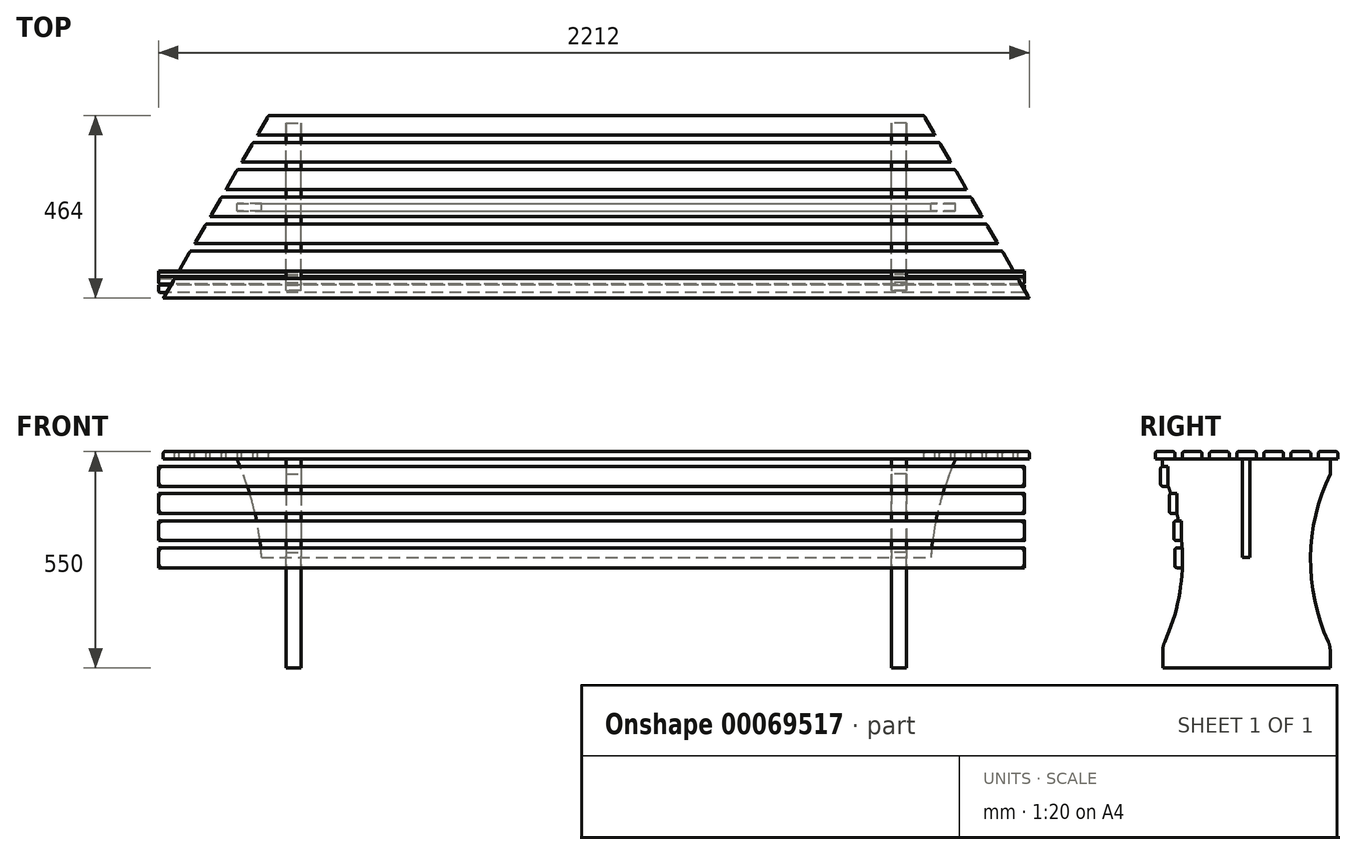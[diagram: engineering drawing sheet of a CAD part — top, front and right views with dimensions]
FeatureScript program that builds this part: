
annotation { "Feature Type Name" : "Feature", "Feature Type Description" : "" }
export const myFeature = defineFeature(function(context is Context, id is Id, definition is map)
    precondition{}
    {
        {
            var Q0;
            Q0=qCreatedBy(makeId("Top.planeOp"),FACE);
            var sketch = newSketch(context, id + "F0", { "sketchPlane" : qUnion([Q0])});
            skLineSegment(sketch, "E0.bottom", {"start": v(-1100, 50) * mm, "end": v(1100, 50) * mm});
            skLineSegment(sketch, "E0.top", {"start": v(-1100, 0) * mm, "end": v(1100, 0) * mm});
            skLineSegment(sketch, "E0.left", {"start": v(-1100, 50) * mm, "end": v(-1100, 0) * mm});
            skLineSegment(sketch, "E0.right", {"start": v(1100, 50) * mm, "end": v(1100, 0) * mm});
            skLineSegment(sketch, "E1.bottom", {"start": v(-1100, 119) * mm, "end": v(1100, 119) * mm});
            skLineSegment(sketch, "E1.top", {"start": v(-1100, 69) * mm, "end": v(1100, 69) * mm});
            skLineSegment(sketch, "E1.left", {"start": v(-1100, 119) * mm, "end": v(-1100, 69) * mm});
            skLineSegment(sketch, "E1.right", {"start": v(1100, 119) * mm, "end": v(1100, 69) * mm});
            skLineSegment(sketch, "E2.bottom", {"start": v(-1100, 188) * mm, "end": v(1100, 188) * mm});
            skLineSegment(sketch, "E2.top", {"start": v(-1100, 138) * mm, "end": v(1100, 138) * mm});
            skLineSegment(sketch, "E2.left", {"start": v(-1100, 188) * mm, "end": v(-1100, 138) * mm});
            skLineSegment(sketch, "E2.right", {"start": v(1100, 188) * mm, "end": v(1100, 138) * mm});
            skLineSegment(sketch, "E3.bottom", {"start": v(-1100, 257) * mm, "end": v(1100, 257) * mm});
            skLineSegment(sketch, "E3.top", {"start": v(-1100, 207) * mm, "end": v(1100, 207) * mm});
            skLineSegment(sketch, "E3.left", {"start": v(-1100, 257) * mm, "end": v(-1100, 207) * mm});
            skLineSegment(sketch, "E3.right", {"start": v(1100, 257) * mm, "end": v(1100, 207) * mm});
            skLineSegment(sketch, "E4.bottom", {"start": v(-1100, 326) * mm, "end": v(1100, 326) * mm});
            skLineSegment(sketch, "E4.top", {"start": v(-1100, 276) * mm, "end": v(1100, 276) * mm});
            skLineSegment(sketch, "E4.left", {"start": v(-1100, 326) * mm, "end": v(-1100, 276) * mm});
            skLineSegment(sketch, "E4.right", {"start": v(1100, 326) * mm, "end": v(1100, 276) * mm});
            skLineSegment(sketch, "E5.bottom", {"start": v(-1100, 395) * mm, "end": v(1100, 395) * mm});
            skLineSegment(sketch, "E5.top", {"start": v(-1100, 345) * mm, "end": v(1100, 345) * mm});
            skLineSegment(sketch, "E5.left", {"start": v(-1100, 395) * mm, "end": v(-1100, 345) * mm});
            skLineSegment(sketch, "E5.right", {"start": v(1100, 395) * mm, "end": v(1100, 345) * mm});
            skLineSegment(sketch, "E6.bottom", {"start": v(-1100, 464) * mm, "end": v(1100, 464) * mm});
            skLineSegment(sketch, "E6.top", {"start": v(-1100, 414) * mm, "end": v(1100, 414) * mm});
            skLineSegment(sketch, "E6.left", {"start": v(-1100, 464) * mm, "end": v(-1100, 414) * mm});
            skLineSegment(sketch, "E6.right", {"start": v(1100, 464) * mm, "end": v(1100, 414) * mm});
            skSolve(sketch);
        }
        {
            var Q0;
            Q0=makeQuery(id+"F0.imprint","IMPRINT",FACE,{"disambiguationData":[TD([[makeQuery(id+"F0.imprint","IMPRINT",EDGE,{"derivedFrom":sQuery(id+"F0.wireOp",EDGE,"E0.bottom")}),-1.0]])]});
            var Q1;
            Q1=makeQuery(id+"F0.imprint","IMPRINT",FACE,{"disambiguationData":[TD([[makeQuery(id+"F0.imprint","IMPRINT",EDGE,{"derivedFrom":sQuery(id+"F0.wireOp",EDGE,"E1.bottom")}),-1.0]])]});
            var Q2;
            Q2=makeQuery(id+"F0.imprint","IMPRINT",FACE,{"disambiguationData":[TD([[makeQuery(id+"F0.imprint","IMPRINT",EDGE,{"derivedFrom":sQuery(id+"F0.wireOp",EDGE,"E2.bottom")}),-1.0]])]});
            var Q3;
            Q3=makeQuery(id+"F0.imprint","IMPRINT",FACE,{"disambiguationData":[TD([[makeQuery(id+"F0.imprint","IMPRINT",EDGE,{"derivedFrom":sQuery(id+"F0.wireOp",EDGE,"E3.bottom")}),-1.0]])]});
            var Q4;
            Q4=makeQuery(id+"F0.imprint","IMPRINT",FACE,{"disambiguationData":[TD([[makeQuery(id+"F0.imprint","IMPRINT",EDGE,{"derivedFrom":sQuery(id+"F0.wireOp",EDGE,"E4.bottom")}),-1.0]])]});
            var Q5;
            Q5=makeQuery(id+"F0.imprint","IMPRINT",FACE,{"disambiguationData":[TD([[makeQuery(id+"F0.imprint","IMPRINT",EDGE,{"derivedFrom":sQuery(id+"F0.wireOp",EDGE,"E5.bottom")}),-1.0]])]});
            var Q6;
            Q6=makeQuery(id+"F0.imprint","IMPRINT",FACE,{"disambiguationData":[TD([[makeQuery(id+"F0.imprint","IMPRINT",EDGE,{"derivedFrom":sQuery(id+"F0.wireOp",EDGE,"E6.bottom")}),-1.0]])]});
            extrude(context, id + "F1", {"entities" : qUnion([Q0, Q1, Q2, Q3, Q4, Q5, Q6]), "depth" : 19 * mm});
        }
        {
            var Q0;
            Q0=qCreatedBy(makeId("Right.planeOp"),FACE);
            cPlane(context, id + "F2", {"entities" : qUnion([Q0]), "cplaneType" : CPlaneType.OFFSET, "offset" : 750 * mm, "width" : 150 * mm, "height" : 150 * mm});
        }
        {
            var Q0;
            Q0=qCreatedBy(id+"F2.planeOp",FACE);
            var sketch = newSketch(context, id + "F3", { "sketchPlane" : qUnion([Q0])});
            skLineSegment(sketch, "E7", {"start": v(19, 0) * mm, "end": v(445, 0) * mm});
            skLineSegment(sketch, "E8", {"start": v(445, 0) * mm, "end": v(445, -38) * mm});
            skLineSegment(sketch, "E9", {"start": v(19, 0) * mm, "end": v(19, -38) * mm});
            skArc(sketch, "E10", {"start": v(19.5, -474) * mm, "mid": v(69.28, -255.94) * mm, "end": v(19, -38) * mm});
            skArc(sketch, "E11", {"start": v(445, -38) * mm, "mid": v(394.72, -255.94) * mm, "end": v(444.5, -474) * mm});
            skLineSegment(sketch, "E12", {"start": v(19.5, -474) * mm, "end": v(19.5, -531) * mm});
            skLineSegment(sketch, "E13", {"start": v(19.5, -531) * mm, "end": v(444.5, -531) * mm});
            skLineSegment(sketch, "E14", {"start": v(444.5, -531) * mm, "end": v(444.5, -474) * mm});
            skSolve(sketch);
        }
        {
            var Q0;
            Q0=makeQuery(id+"F3.imprint","IMPRINT",FACE,{"disambiguationData":[TD([[makeQuery(id+"F3.imprint","IMPRINT",EDGE,{"derivedFrom":sQuery(id+"F3.wireOp",EDGE,"E7")}),-1.0]])]});
            extrude(context, id + "F4", {"entities" : qUnion([Q0]), "depth" : 38 * mm});
        }
        {
            var Q0;
            Q0=makeQuery(id+"F4.opExtrude","SWEPT_BODY",BODY,{"disambiguationData":[OSD([sQuery(id+"F3.wireOp",EDGE,"E7"),sQuery(id+"F3.wireOp",EDGE,"E8"),sQuery(id+"F3.wireOp",EDGE,"E9"),sQuery(id+"F3.wireOp",EDGE,"E10"),sQuery(id+"F3.wireOp",EDGE,"E11"),sQuery(id+"F3.wireOp",EDGE,"E12"),sQuery(id+"F3.wireOp",EDGE,"E13"),sQuery(id+"F3.wireOp",EDGE,"E14")])]});
            var Q1;
            Q1=qCreatedBy(makeId("Right.planeOp"),FACE);
            mirror(context, id + "F5", {"entities" : qUnion([Q0]), "mirrorPlane" : qUnion([Q1])});
        }
        {
            var Q0;
            Q0=qCreatedBy(makeId("Front.planeOp"),FACE);
            cPlane(context, id + "F6", {"entities" : qUnion([Q0]), "cplaneType" : CPlaneType.OFFSET, "offset" : 240 * mm, "oppositeDirection" : true, "width" : 150 * mm, "height" : 150 * mm});
        }
        {
            var Q0;
            Q0=qCreatedBy(id+"F6.planeOp",FACE);
            var sketch = newSketch(context, id + "F7", { "sketchPlane" : qUnion([Q0])});
            skLineSegment(sketch, "E15", {"start": v(-913, 0) * mm, "end": v(913, 0) * mm});
            skArc(sketch, "E16", {"start": v(-850, -250) * mm, "mid": v(-870.68, -122.27) * mm, "end": v(-913, 0) * mm});
            skArc(sketch, "E17", {"start": v(913, 0) * mm, "mid": v(870.68, -122.27) * mm, "end": v(850, -250) * mm});
            skLineSegment(sketch, "E18", {"start": v(-850, -250) * mm, "end": v(850, -250) * mm});
            skSolve(sketch);
        }
        {
            var Q0;
            Q0=makeQuery(id+"F7.imprint","IMPRINT",FACE,{"disambiguationData":[TD([[makeQuery(id+"F7.imprint","IMPRINT",EDGE,{"derivedFrom":sQuery(id+"F7.wireOp",EDGE,"E15")}),-1.0]])]});
            extrude(context, id + "F8", {"entities" : qUnion([Q0]), "depth" : 19 * mm});
        }
        {
            var Q0;
            Q0=makeQuery(id+"F1.opExtrude","CAP_FACE",FACE,{"disambiguationData":[OSD([sQuery(id+"F0.wireOp",EDGE,"E6.bottom"),sQuery(id+"F0.wireOp",EDGE,"E6.top"),sQuery(id+"F0.wireOp",EDGE,"E6.left"),sQuery(id+"F0.wireOp",EDGE,"E6.right")])],"isStart":false});
            var sketch = newSketch(context, id + "F9", { "sketchPlane" : qUnion([Q0])});
            skLineSegment(sketch, "E19", {"start": v(-1100, 0) * mm, "end": v(-1100, 464) * mm});
            skLineSegment(sketch, "E20", {"start": v(-1100, 464) * mm, "end": v(-832.1, 464) * mm});
            skLineSegment(sketch, "E21", {"start": v(-832.1, 464) * mm, "end": v(-1100, 0) * mm});
            skLineSegment(sketch, "E22", {"start": v(1100, 0) * mm, "end": v(1100, 464) * mm});
            skLineSegment(sketch, "E23", {"start": v(1100, 464) * mm, "end": v(832.1, 464) * mm});
            skLineSegment(sketch, "E24", {"start": v(832.1, 464) * mm, "end": v(1100, 0) * mm});
            skSolve(sketch);
        }
        {
            var Q0;
            Q0 = qSketchRegion(id + "F9", true);
            extrude(context, id + "F10", {"entities" : qUnion([Q0]), "operationType" : NewBodyOperationType.REMOVE, "endBound" : BoundingType.THROUGH_ALL, "oppositeDirection" : true, "depth" : 25 * mm});
        }
        {
            var Q0;
            Q0=makeQuery(id+"F1.opExtrude","CAP_EDGE",EDGE,{"disambiguationData":[OSD([sQuery(id+"F0.wireOp",EDGE,"E0.top")])],"isStart":false});
            var Q1;
            Q1=makeQuery(id+"F10.boolean.opBoolean","COPY",EDGE,{"disambiguationData":[OD(0.0)],"derivedFrom":makeQuery(id+"F10.opExtrude","CAP_EDGE",EDGE,{"disambiguationData":[OSD([sQuery(id+"F9.wireOp",EDGE,"E24")])],"isStart":true})});
            var Q2;
            Q2=makeQuery(id+"F1.opExtrude","CAP_EDGE",EDGE,{"disambiguationData":[OSD([sQuery(id+"F0.wireOp",EDGE,"E0.bottom")])],"isStart":false});
            var Q3;
            Q3=makeQuery(id+"F1.opExtrude","CAP_EDGE",EDGE,{"disambiguationData":[OSD([sQuery(id+"F0.wireOp",EDGE,"E1.top")])],"isStart":false});
            var Q4;
            Q4=makeQuery(id+"F10.boolean.opBoolean","COPY",EDGE,{"disambiguationData":[OD(2.0)],"derivedFrom":makeQuery(id+"F10.opExtrude","CAP_EDGE",EDGE,{"disambiguationData":[OSD([sQuery(id+"F9.wireOp",EDGE,"E24")])],"isStart":true})});
            var Q5;
            Q5=makeQuery(id+"F1.opExtrude","CAP_EDGE",EDGE,{"disambiguationData":[OSD([sQuery(id+"F0.wireOp",EDGE,"E1.bottom")])],"isStart":false});
            var Q6;
            Q6=makeQuery(id+"F1.opExtrude","CAP_EDGE",EDGE,{"disambiguationData":[OSD([sQuery(id+"F0.wireOp",EDGE,"E2.top")])],"isStart":false});
            var Q7;
            Q7=makeQuery(id+"F10.boolean.opBoolean","COPY",EDGE,{"disambiguationData":[OD(3.0)],"derivedFrom":makeQuery(id+"F10.opExtrude","CAP_EDGE",EDGE,{"disambiguationData":[OSD([sQuery(id+"F9.wireOp",EDGE,"E24")])],"isStart":true})});
            var Q8;
            Q8=makeQuery(id+"F1.opExtrude","CAP_EDGE",EDGE,{"disambiguationData":[OSD([sQuery(id+"F0.wireOp",EDGE,"E2.bottom")])],"isStart":false});
            var Q9;
            Q9=makeQuery(id+"F1.opExtrude","CAP_EDGE",EDGE,{"disambiguationData":[OSD([sQuery(id+"F0.wireOp",EDGE,"E3.top")])],"isStart":false});
            var Q10;
            Q10=makeQuery(id+"F1.opExtrude","CAP_EDGE",EDGE,{"disambiguationData":[OSD([sQuery(id+"F0.wireOp",EDGE,"E3.bottom")])],"isStart":false});
            var Q11;
            Q11=makeQuery(id+"F10.boolean.opBoolean","COPY",EDGE,{"disambiguationData":[OD(4.0)],"derivedFrom":makeQuery(id+"F10.opExtrude","CAP_EDGE",EDGE,{"disambiguationData":[OSD([sQuery(id+"F9.wireOp",EDGE,"E24")])],"isStart":true})});
            var Q12;
            Q12=makeQuery(id+"F1.opExtrude","CAP_EDGE",EDGE,{"disambiguationData":[OSD([sQuery(id+"F0.wireOp",EDGE,"E4.top")])],"isStart":false});
            var Q13;
            Q13=makeQuery(id+"F1.opExtrude","CAP_EDGE",EDGE,{"disambiguationData":[OSD([sQuery(id+"F0.wireOp",EDGE,"E4.bottom")])],"isStart":false});
            var Q14;
            Q14=makeQuery(id+"F10.boolean.opBoolean","COPY",EDGE,{"disambiguationData":[OD(5.0)],"derivedFrom":makeQuery(id+"F10.opExtrude","CAP_EDGE",EDGE,{"disambiguationData":[OSD([sQuery(id+"F9.wireOp",EDGE,"E24")])],"isStart":true})});
            var Q15;
            Q15=makeQuery(id+"F1.opExtrude","CAP_EDGE",EDGE,{"disambiguationData":[OSD([sQuery(id+"F0.wireOp",EDGE,"E5.top")])],"isStart":false});
            var Q16;
            Q16=makeQuery(id+"F1.opExtrude","CAP_EDGE",EDGE,{"disambiguationData":[OSD([sQuery(id+"F0.wireOp",EDGE,"E5.bottom")])],"isStart":false});
            var Q17;
            Q17=makeQuery(id+"F10.boolean.opBoolean","COPY",EDGE,{"disambiguationData":[OD(6.0)],"derivedFrom":makeQuery(id+"F10.opExtrude","CAP_EDGE",EDGE,{"disambiguationData":[OSD([sQuery(id+"F9.wireOp",EDGE,"E24")])],"isStart":true})});
            var Q18;
            Q18=makeQuery(id+"F1.opExtrude","CAP_EDGE",EDGE,{"disambiguationData":[OSD([sQuery(id+"F0.wireOp",EDGE,"E6.top")])],"isStart":false});
            var Q19;
            Q19=makeQuery(id+"F10.boolean.opBoolean","COPY",EDGE,{"disambiguationData":[OD(1.0)],"derivedFrom":makeQuery(id+"F10.opExtrude","CAP_EDGE",EDGE,{"disambiguationData":[OSD([sQuery(id+"F9.wireOp",EDGE,"E24")])],"isStart":true})});
            var Q20;
            Q20=makeQuery(id+"F1.opExtrude","CAP_EDGE",EDGE,{"disambiguationData":[OSD([sQuery(id+"F0.wireOp",EDGE,"E6.bottom")])],"isStart":false});
            var Q21;
            Q21=makeQuery(id+"F10.boolean.opBoolean","COPY",EDGE,{"disambiguationData":[OD(0.0)],"derivedFrom":makeQuery(id+"F10.opExtrude","CAP_EDGE",EDGE,{"disambiguationData":[OSD([sQuery(id+"F9.wireOp",EDGE,"E21")])],"isStart":true})});
            var Q22;
            Q22=makeQuery(id+"F10.boolean.opBoolean","COPY",EDGE,{"disambiguationData":[OD(2.0)],"derivedFrom":makeQuery(id+"F10.opExtrude","CAP_EDGE",EDGE,{"disambiguationData":[OSD([sQuery(id+"F9.wireOp",EDGE,"E21")])],"isStart":true})});
            var Q23;
            Q23=makeQuery(id+"F10.boolean.opBoolean","COPY",EDGE,{"disambiguationData":[OD(3.0)],"derivedFrom":makeQuery(id+"F10.opExtrude","CAP_EDGE",EDGE,{"disambiguationData":[OSD([sQuery(id+"F9.wireOp",EDGE,"E21")])],"isStart":true})});
            var Q24;
            Q24=makeQuery(id+"F10.boolean.opBoolean","COPY",EDGE,{"disambiguationData":[OD(4.0)],"derivedFrom":makeQuery(id+"F10.opExtrude","CAP_EDGE",EDGE,{"disambiguationData":[OSD([sQuery(id+"F9.wireOp",EDGE,"E21")])],"isStart":true})});
            var Q25;
            Q25=makeQuery(id+"F10.boolean.opBoolean","COPY",EDGE,{"disambiguationData":[OD(5.0)],"derivedFrom":makeQuery(id+"F10.opExtrude","CAP_EDGE",EDGE,{"disambiguationData":[OSD([sQuery(id+"F9.wireOp",EDGE,"E21")])],"isStart":true})});
            var Q26;
            Q26=makeQuery(id+"F10.boolean.opBoolean","COPY",EDGE,{"disambiguationData":[OD(6.0)],"derivedFrom":makeQuery(id+"F10.opExtrude","CAP_EDGE",EDGE,{"disambiguationData":[OSD([sQuery(id+"F9.wireOp",EDGE,"E21")])],"isStart":true})});
            var Q27;
            Q27=makeQuery(id+"F10.boolean.opBoolean","COPY",EDGE,{"disambiguationData":[OD(1.0)],"derivedFrom":makeQuery(id+"F10.opExtrude","CAP_EDGE",EDGE,{"disambiguationData":[OSD([sQuery(id+"F9.wireOp",EDGE,"E21")])],"isStart":true})});
            fillet(context, id + "F11", {"entities" : qUnion([Q0, Q1, Q2, Q3, Q4, Q5, Q6, Q7, Q8, Q9, Q10, Q11, Q12, Q13, Q14, Q15, Q16, Q17, Q18, Q19, Q20, Q21, Q22, Q23, Q24, Q25, Q26, Q27]), "radius" : 5 * mm, "tangentPropagation" : true, "allowEdgeOverflow" : false});
        }
        {
            var Q0;
            Q0=makeQuery(id+"F4.opExtrude","CAP_FACE",FACE,{"disambiguationData":[OSD([sQuery(id+"F3.wireOp",EDGE,"E7"),sQuery(id+"F3.wireOp",EDGE,"E8"),sQuery(id+"F3.wireOp",EDGE,"E9"),sQuery(id+"F3.wireOp",EDGE,"E10"),sQuery(id+"F3.wireOp",EDGE,"E11"),sQuery(id+"F3.wireOp",EDGE,"E12"),sQuery(id+"F3.wireOp",EDGE,"E13"),sQuery(id+"F3.wireOp",EDGE,"E14")])],"isStart":false});
            var sketch = newSketch(context, id + "F12", { "sketchPlane" : qUnion([Q0])});
            skLineSegment(sketch, "E25.bottom", {"start": v(32.78, -69) * mm, "end": v(13.78, -69) * mm});
            skLineSegment(sketch, "E25.top", {"start": v(32.78, -19) * mm, "end": v(13.78, -19) * mm});
            skLineSegment(sketch, "E25.left", {"start": v(32.78, -69) * mm, "end": v(32.78, -19) * mm});
            skLineSegment(sketch, "E25.right", {"start": v(13.78, -69) * mm, "end": v(13.78, -19) * mm});
            skLineSegment(sketch, "E26.bottom", {"start": v(55.03, -138) * mm, "end": v(36.03, -138) * mm});
            skLineSegment(sketch, "E26.top", {"start": v(55.03, -88) * mm, "end": v(36.03, -88) * mm});
            skLineSegment(sketch, "E26.left", {"start": v(55.03, -138) * mm, "end": v(55.03, -88) * mm});
            skLineSegment(sketch, "E26.right", {"start": v(36.03, -138) * mm, "end": v(36.03, -88) * mm});
            skLineSegment(sketch, "E27.bottom", {"start": v(66.82, -207) * mm, "end": v(47.82, -207) * mm});
            skLineSegment(sketch, "E27.top", {"start": v(66.82, -157) * mm, "end": v(47.82, -157) * mm});
            skLineSegment(sketch, "E27.left", {"start": v(66.82, -207) * mm, "end": v(66.82, -157) * mm});
            skLineSegment(sketch, "E27.right", {"start": v(47.82, -207) * mm, "end": v(47.82, -157) * mm});
            skLineSegment(sketch, "E28.bottom", {"start": v(68.9, -276) * mm, "end": v(49.9, -276) * mm});
            skLineSegment(sketch, "E28.top", {"start": v(68.9, -226) * mm, "end": v(49.9, -226) * mm});
            skLineSegment(sketch, "E28.left", {"start": v(68.9, -276) * mm, "end": v(68.9, -226) * mm});
            skLineSegment(sketch, "E28.right", {"start": v(49.9, -276) * mm, "end": v(49.9, -226) * mm});
            skSolve(sketch);
        }
        {
            var Q0;
            Q0 = qSketchRegion(id + "F12", true);
            extrude(context, id + "F13", {"entities" : qUnion([Q0]), "operationType" : NewBodyOperationType.REMOVE, "endBound" : BoundingType.THROUGH_ALL, "oppositeDirection" : true, "depth" : 25 * mm});
        }
        {
            var Q0;
            Q0 = qSketchRegion(id + "F12", true);
            extrude(context, id + "F14", {"entities" : qUnion([Q0]), "depth" : 300 * mm, "hasSecondDirection" : true, "secondDirectionOppositeDirection" : true, "secondDirectionDepth" : 1900 * mm});
        }
        {
            var Q0;
            Q0=makeQuery(id+"F14.opExtrude","SWEPT_EDGE",EDGE,{"disambiguationData":[OSD([sQuery(id+"F12.wireOp",EDGE,"E25.top"),sQuery(id+"F12.wireOp",EDGE,"E25.right")])]});
            var Q1;
            Q1=makeQuery(id+"F14.opExtrude","CAP_EDGE",EDGE,{"disambiguationData":[OSD([sQuery(id+"F12.wireOp",EDGE,"E25.right")])],"isStart":false});
            var Q2;
            Q2=makeQuery(id+"F14.opExtrude","SWEPT_EDGE",EDGE,{"disambiguationData":[OSD([sQuery(id+"F12.wireOp",EDGE,"E25.bottom"),sQuery(id+"F12.wireOp",EDGE,"E25.right")])]});
            var Q3;
            Q3=makeQuery(id+"F14.opExtrude","SWEPT_EDGE",EDGE,{"disambiguationData":[OSD([sQuery(id+"F12.wireOp",EDGE,"E26.top"),sQuery(id+"F12.wireOp",EDGE,"E26.right")])]});
            var Q4;
            Q4=makeQuery(id+"F14.opExtrude","CAP_EDGE",EDGE,{"disambiguationData":[OSD([sQuery(id+"F12.wireOp",EDGE,"E26.right")])],"isStart":false});
            var Q5;
            Q5=makeQuery(id+"F14.opExtrude","SWEPT_EDGE",EDGE,{"disambiguationData":[OSD([sQuery(id+"F12.wireOp",EDGE,"E26.bottom"),sQuery(id+"F12.wireOp",EDGE,"E26.right")])]});
            var Q6;
            Q6=makeQuery(id+"F14.opExtrude","SWEPT_EDGE",EDGE,{"disambiguationData":[OSD([sQuery(id+"F12.wireOp",EDGE,"E27.top"),sQuery(id+"F12.wireOp",EDGE,"E27.right")])]});
            var Q7;
            Q7=makeQuery(id+"F14.opExtrude","CAP_EDGE",EDGE,{"disambiguationData":[OSD([sQuery(id+"F12.wireOp",EDGE,"E27.right")])],"isStart":false});
            var Q8;
            Q8=makeQuery(id+"F14.opExtrude","SWEPT_EDGE",EDGE,{"disambiguationData":[OSD([sQuery(id+"F12.wireOp",EDGE,"E27.bottom"),sQuery(id+"F12.wireOp",EDGE,"E27.right")])]});
            var Q9;
            Q9=makeQuery(id+"F14.opExtrude","SWEPT_EDGE",EDGE,{"disambiguationData":[OSD([sQuery(id+"F12.wireOp",EDGE,"E28.bottom"),sQuery(id+"F12.wireOp",EDGE,"E28.right")])]});
            var Q10;
            Q10=makeQuery(id+"F14.opExtrude","SWEPT_EDGE",EDGE,{"disambiguationData":[OSD([sQuery(id+"F12.wireOp",EDGE,"E28.top"),sQuery(id+"F12.wireOp",EDGE,"E28.right")])]});
            var Q11;
            Q11=makeQuery(id+"F14.opExtrude","CAP_EDGE",EDGE,{"disambiguationData":[OSD([sQuery(id+"F12.wireOp",EDGE,"E28.right")])],"isStart":false});
            var Q12;
            Q12=makeQuery(id+"F14.opExtrude","CAP_EDGE",EDGE,{"disambiguationData":[OSD([sQuery(id+"F12.wireOp",EDGE,"E25.right")])],"isStart":true});
            var Q13;
            Q13=makeQuery(id+"F14.opExtrude","CAP_EDGE",EDGE,{"disambiguationData":[OSD([sQuery(id+"F12.wireOp",EDGE,"E26.right")])],"isStart":true});
            var Q14;
            Q14=makeQuery(id+"F14.opExtrude","CAP_EDGE",EDGE,{"disambiguationData":[OSD([sQuery(id+"F12.wireOp",EDGE,"E27.right")])],"isStart":true});
            var Q15;
            Q15=makeQuery(id+"F14.opExtrude","CAP_EDGE",EDGE,{"disambiguationData":[OSD([sQuery(id+"F12.wireOp",EDGE,"E28.right")])],"isStart":true});
            fillet(context, id + "F15", {"entities" : qUnion([Q0, Q1, Q2, Q3, Q4, Q5, Q6, Q7, Q8, Q9, Q10, Q11, Q12, Q13, Q14, Q15]), "radius" : 5 * mm, "tangentPropagation" : true, "allowEdgeOverflow" : false});
        }
        {
            var Q0;
            Q0=makeQuery(id+"F4.opExtrude","SWEPT_EDGE",EDGE,{"disambiguationData":[OSD([sQuery(id+"F3.wireOp",EDGE,"E10"),sQuery(id+"F3.wireOp",EDGE,"E12")])]});
            var Q1;
            Q1=makeQuery(id+"F5.opPattern","COPY",EDGE,{"derivedFrom":makeQuery(id+"F4.opExtrude","SWEPT_EDGE",EDGE,{"disambiguationData":[OSD([sQuery(id+"F3.wireOp",EDGE,"E10"),sQuery(id+"F3.wireOp",EDGE,"E12")])]}),"instanceName":"1"});
            var Q2;
            Q2=makeQuery(id+"F4.opExtrude","SWEPT_EDGE",EDGE,{"disambiguationData":[OSD([sQuery(id+"F3.wireOp",EDGE,"E11"),sQuery(id+"F3.wireOp",EDGE,"E14")])]});
            var Q3;
            Q3=makeQuery(id+"F5.opPattern","COPY",EDGE,{"derivedFrom":makeQuery(id+"F4.opExtrude","SWEPT_EDGE",EDGE,{"disambiguationData":[OSD([sQuery(id+"F3.wireOp",EDGE,"E11"),sQuery(id+"F3.wireOp",EDGE,"E14")])]}),"instanceName":"1"});
            fillet(context, id + "F16", {"entities" : qUnion([Q0, Q1, Q2, Q3]), "radius" : 50 * mm, "tangentPropagation" : true, "allowEdgeOverflow" : false});
        }
    });
